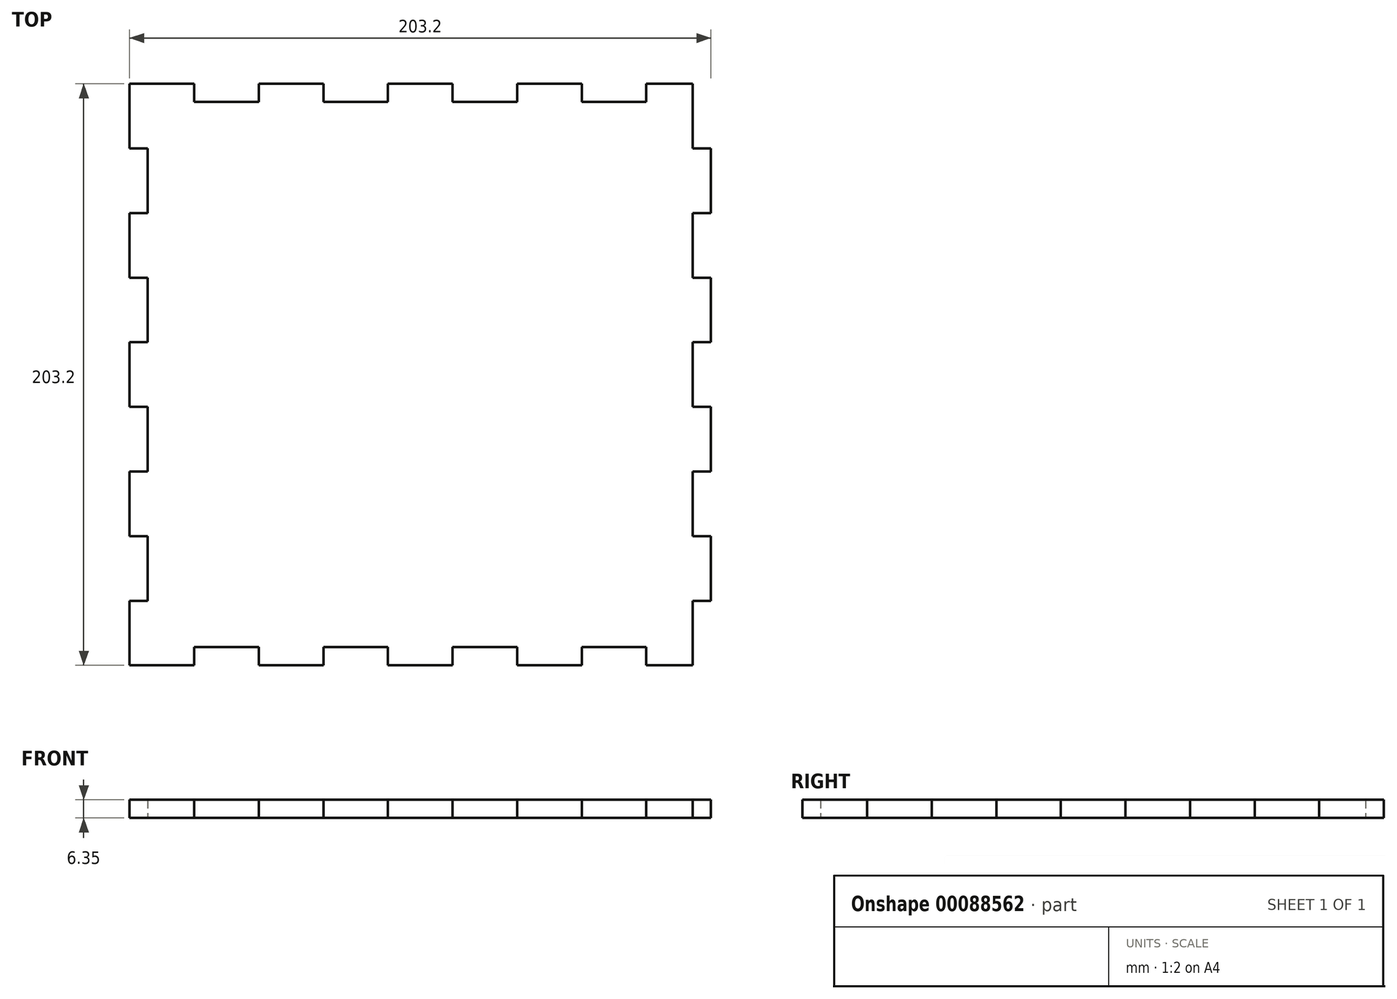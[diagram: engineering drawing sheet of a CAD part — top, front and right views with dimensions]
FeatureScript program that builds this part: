
annotation { "Feature Type Name" : "Feature", "Feature Type Description" : "" }
export const myFeature = defineFeature(function(context is Context, id is Id, definition is map)
    precondition{}
    {
        {
            var Q0;
            Q0=qCreatedBy(makeId("Top.planeOp"),FACE);
            var sketch = newSketch(context, id + "F0", { "sketchPlane" : qUnion([Q0])});
            skLineSegment(sketch, "E0.bottom", {"start": v(-101.6, 101.6) * mm, "end": v(101.6, 101.6) * mm, "construction": true});
            skLineSegment(sketch, "E0.top", {"start": v(-101.6, -101.6) * mm, "end": v(101.6, -101.6) * mm, "construction": true});
            skLineSegment(sketch, "E0.left", {"start": v(-101.6, 101.6) * mm, "end": v(-101.6, -101.6) * mm, "construction": true});
            skLineSegment(sketch, "E0.right", {"start": v(101.6, 101.6) * mm, "end": v(101.6, -101.6) * mm, "construction": true});
            skPoint(sketch, "E0.middle", {"position": v(0, 0) * mm});
            skLineSegment(sketch, "E1.bottom", {"start": v(-95.25, 95.25) * mm, "end": v(95.25, 95.25) * mm, "construction": true});
            skLineSegment(sketch, "E1.top", {"start": v(-95.25, -95.25) * mm, "end": v(95.25, -95.25) * mm, "construction": true});
            skLineSegment(sketch, "E1.left", {"start": v(-95.25, 95.25) * mm, "end": v(-95.25, -95.25) * mm, "construction": true});
            skLineSegment(sketch, "E1.right", {"start": v(95.25, 95.25) * mm, "end": v(95.25, -95.25) * mm, "construction": true});
            skLineSegment(sketch, "E2", {"start": v(-79.02, 101.6) * mm, "end": v(-79.02, 95.25) * mm});
            skLineSegment(sketch, "E3", {"start": v(-56.44, 101.6) * mm, "end": v(-56.44, 95.25) * mm});
            skLineSegment(sketch, "E4", {"start": v(-33.87, 101.6) * mm, "end": v(-33.87, 95.25) * mm});
            skLineSegment(sketch, "E5", {"start": v(-11.29, 101.6) * mm, "end": v(-11.29, 95.25) * mm});
            skLineSegment(sketch, "E6", {"start": v(11.29, 101.6) * mm, "end": v(11.29, 95.25) * mm});
            skLineSegment(sketch, "E7", {"start": v(33.87, 101.6) * mm, "end": v(33.87, 95.25) * mm});
            skLineSegment(sketch, "E8", {"start": v(56.44, 101.6) * mm, "end": v(56.44, 95.25) * mm});
            skLineSegment(sketch, "E9", {"start": v(79.02, 101.6) * mm, "end": v(79.02, 95.25) * mm});
            skLineSegment(sketch, "E10", {"start": v(-101.6, 101.6) * mm, "end": v(-79.02, 101.6) * mm});
            skLineSegment(sketch, "E11", {"start": v(-79.02, 95.25) * mm, "end": v(-56.44, 95.25) * mm});
            skLineSegment(sketch, "E12", {"start": v(-56.44, 101.6) * mm, "end": v(-33.87, 101.6) * mm});
            skLineSegment(sketch, "E13", {"start": v(-33.87, 95.25) * mm, "end": v(-11.29, 95.25) * mm});
            skLineSegment(sketch, "E14", {"start": v(-11.29, 101.6) * mm, "end": v(11.29, 101.6) * mm});
            skLineSegment(sketch, "E15", {"start": v(11.29, 95.25) * mm, "end": v(33.87, 95.25) * mm});
            skLineSegment(sketch, "E16", {"start": v(33.87, 101.6) * mm, "end": v(56.44, 101.6) * mm});
            skLineSegment(sketch, "E17", {"start": v(56.44, 95.25) * mm, "end": v(79.02, 95.25) * mm});
            skLineSegment(sketch, "E18", {"start": v(79.02, 101.6) * mm, "end": v(95.25, 101.6) * mm});
            skLineSegment(sketch, "E19", {"start": v(95.25, 101.6) * mm, "end": v(95.25, 79.02) * mm});
            skLineSegment(sketch, "E20", {"start": v(95.25, 79.02) * mm, "end": v(101.6, 79.02) * mm});
            skLineSegment(sketch, "E21", {"start": v(101.6, 79.02) * mm, "end": v(101.6, 56.44) * mm});
            skLineSegment(sketch, "E22", {"start": v(101.6, 56.44) * mm, "end": v(95.25, 56.44) * mm});
            skLineSegment(sketch, "E23", {"start": v(95.25, 56.44) * mm, "end": v(95.25, 33.87) * mm});
            skLineSegment(sketch, "E24", {"start": v(95.25, 33.87) * mm, "end": v(101.6, 33.87) * mm});
            skLineSegment(sketch, "E25", {"start": v(101.6, 33.87) * mm, "end": v(101.6, 11.29) * mm});
            skLineSegment(sketch, "E26", {"start": v(101.6, 11.29) * mm, "end": v(95.25, 11.29) * mm});
            skLineSegment(sketch, "E27", {"start": v(95.25, 11.29) * mm, "end": v(95.25, 0) * mm});
            skLineSegment(sketch, "E28", {"start": v(-101.6, 101.6) * mm, "end": v(-101.6, 79.02) * mm});
            skLineSegment(sketch, "E29", {"start": v(-101.6, 79.02) * mm, "end": v(-95.25, 79.02) * mm});
            skLineSegment(sketch, "E30", {"start": v(-95.25, 79.02) * mm, "end": v(-95.25, 56.44) * mm});
            skLineSegment(sketch, "E31", {"start": v(-95.25, 56.44) * mm, "end": v(-101.6, 56.44) * mm});
            skLineSegment(sketch, "E32", {"start": v(-101.6, 56.44) * mm, "end": v(-101.6, 33.87) * mm});
            skLineSegment(sketch, "E33", {"start": v(-101.6, 33.87) * mm, "end": v(-95.25, 33.87) * mm});
            skLineSegment(sketch, "E34", {"start": v(-95.25, 33.87) * mm, "end": v(-95.25, 11.29) * mm});
            skLineSegment(sketch, "E35", {"start": v(-95.25, 11.29) * mm, "end": v(-101.6, 11.29) * mm});
            skLineSegment(sketch, "E36", {"start": v(-101.6, 11.29) * mm, "end": v(-101.6, 0) * mm});
            skLineSegment(sketch, "E37.MirrorCS", {"start": v(101.6, -11.29) * mm, "end": v(95.25, -11.29) * mm});
            skLineSegment(sketch, "E38.MirrorCS", {"start": v(-101.6, -101.6) * mm, "end": v(-79.02, -101.6) * mm});
            skLineSegment(sketch, "E39.MirrorCS", {"start": v(-101.6, -101.6) * mm, "end": v(-101.6, -79.02) * mm});
            skLineSegment(sketch, "E40.MirrorCS", {"start": v(-56.44, -101.6) * mm, "end": v(-33.87, -101.6) * mm});
            skLineSegment(sketch, "E41.MirrorCS", {"start": v(-95.25, -79.02) * mm, "end": v(-95.25, -56.44) * mm});
            skLineSegment(sketch, "E42.MirrorCS", {"start": v(95.25, -56.44) * mm, "end": v(95.25, -33.87) * mm});
            skLineSegment(sketch, "E43.MirrorCS", {"start": v(101.6, -56.44) * mm, "end": v(95.25, -56.44) * mm});
            skLineSegment(sketch, "E44.MirrorCS", {"start": v(-33.87, -101.6) * mm, "end": v(-33.87, -95.25) * mm});
            skLineSegment(sketch, "E45.MirrorCS", {"start": v(-11.29, -101.6) * mm, "end": v(11.29, -101.6) * mm});
            skLineSegment(sketch, "E46.MirrorCS", {"start": v(11.29, -101.6) * mm, "end": v(11.29, -95.25) * mm});
            skLineSegment(sketch, "E47.MirrorCS", {"start": v(11.29, -95.25) * mm, "end": v(33.87, -95.25) * mm});
            skLineSegment(sketch, "E48.MirrorCS", {"start": v(95.25, -79.02) * mm, "end": v(101.6, -79.02) * mm});
            skLineSegment(sketch, "E49.MirrorCS", {"start": v(95.25, -33.87) * mm, "end": v(101.6, -33.87) * mm});
            skLineSegment(sketch, "E50.MirrorCS", {"start": v(-101.6, -11.29) * mm, "end": v(-101.6, 0) * mm});
            skLineSegment(sketch, "E51.MirrorCS", {"start": v(-79.02, -95.25) * mm, "end": v(-56.44, -95.25) * mm});
            skLineSegment(sketch, "E52.MirrorCS", {"start": v(-33.87, -95.25) * mm, "end": v(-11.29, -95.25) * mm});
            skLineSegment(sketch, "E53.MirrorCS", {"start": v(101.6, -79.02) * mm, "end": v(101.6, -56.44) * mm});
            skLineSegment(sketch, "E54.MirrorCS", {"start": v(-11.29, -101.6) * mm, "end": v(-11.29, -95.25) * mm});
            skLineSegment(sketch, "E55.MirrorCS", {"start": v(-101.6, -33.87) * mm, "end": v(-95.25, -33.87) * mm});
            skLineSegment(sketch, "E56.MirrorCS", {"start": v(79.02, -101.6) * mm, "end": v(79.02, -95.25) * mm});
            skLineSegment(sketch, "E57.MirrorCS", {"start": v(-95.25, -56.44) * mm, "end": v(-101.6, -56.44) * mm});
            skLineSegment(sketch, "E58.MirrorCS", {"start": v(101.6, -33.87) * mm, "end": v(101.6, -11.29) * mm});
            skLineSegment(sketch, "E59.MirrorCS", {"start": v(-95.25, -11.29) * mm, "end": v(-101.6, -11.29) * mm});
            skLineSegment(sketch, "E60.MirrorCS", {"start": v(95.25, -101.6) * mm, "end": v(95.25, -79.02) * mm});
            skLineSegment(sketch, "E61.MirrorCS", {"start": v(79.02, -101.6) * mm, "end": v(95.25, -101.6) * mm});
            skLineSegment(sketch, "E62.MirrorCS", {"start": v(-56.44, -101.6) * mm, "end": v(-56.44, -95.25) * mm});
            skLineSegment(sketch, "E63.MirrorCS", {"start": v(-101.6, -79.02) * mm, "end": v(-95.25, -79.02) * mm});
            skLineSegment(sketch, "E64.MirrorCS", {"start": v(33.87, -101.6) * mm, "end": v(33.87, -95.25) * mm});
            skLineSegment(sketch, "E65.MirrorCS", {"start": v(-95.25, -33.87) * mm, "end": v(-95.25, -11.29) * mm});
            skLineSegment(sketch, "E66.MirrorCS", {"start": v(-79.02, -101.6) * mm, "end": v(-79.02, -95.25) * mm});
            skLineSegment(sketch, "E67.MirrorCS", {"start": v(95.25, -11.29) * mm, "end": v(95.25, 0) * mm});
            skLineSegment(sketch, "E68.MirrorCS", {"start": v(-101.6, -56.44) * mm, "end": v(-101.6, -33.87) * mm});
            skLineSegment(sketch, "E69.MirrorCS", {"start": v(33.87, -101.6) * mm, "end": v(56.44, -101.6) * mm});
            skLineSegment(sketch, "E70.MirrorCS", {"start": v(56.44, -95.25) * mm, "end": v(79.02, -95.25) * mm});
            skLineSegment(sketch, "E71.MirrorCS", {"start": v(56.44, -101.6) * mm, "end": v(56.44, -95.25) * mm});
            skSolve(sketch);
        }
        {
            var Q0;
            Q0=makeQuery(id+"F0.imprint","IMPRINT",FACE,{"disambiguationData":[TD([[makeQuery(id+"F0.imprint","IMPRINT",EDGE,{"derivedFrom":sQuery(id+"F0.wireOp",EDGE,"E2")}),-1.0]])]});
            extrude(context, id + "F1", {"entities" : qUnion([Q0]), "depth" : 6.35 * mm});
        }
    });
